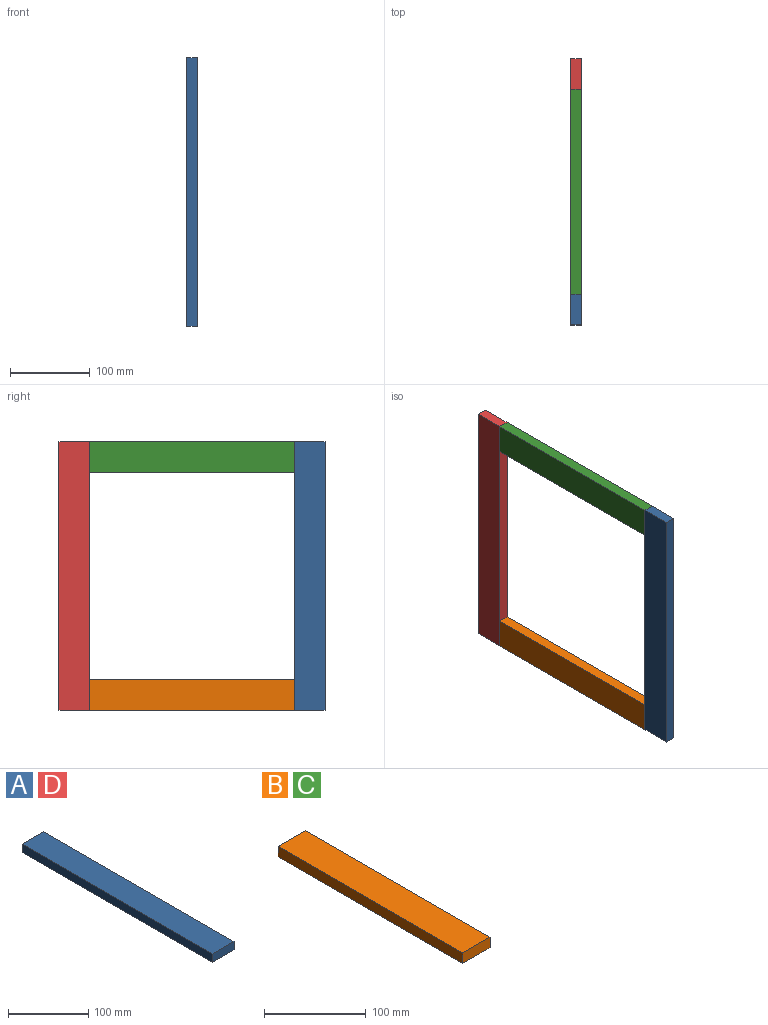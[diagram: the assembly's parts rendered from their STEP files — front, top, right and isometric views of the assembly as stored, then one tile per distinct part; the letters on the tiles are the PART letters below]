
ASSEMBLY  parts=4 mates=9
PART A: 6 faces, bbox 38.1x336.6x12.7 mm
  f0: plane 336.55x12.7mm, normal (-1,0,0), area 4274.2mm2, adj f1,f3,f4,f5
  f1: plane 336.55x38.1mm, normal (0,0,-1), area 12822.6mm2, adj f0,f2,f4,f5
  f2: plane 336.55x12.7mm, normal (1,0,0), area 4274.2mm2, adj f1,f3,f4,f5
  f3: plane 336.55x38.1mm, normal (0,0,1), area 12822.6mm2, adj f0,f2,f4,f5
  f4: plane 38.1x12.7mm, normal (0,-1,0), area 483.9mm2, adj f0,f1,f2,f3
  f5: plane 38.1x12.7mm, normal (0,1,0), area 483.9mm2, adj f0,f1,f2,f3
PART B: 6 faces, bbox 38.1x257.2x12.7 mm
  f0: plane 257.18x38.1mm, normal (0,0,1), area 9798.4mm2, adj f1,f3,f4,f5
  f1: plane 257.18x12.7mm, normal (-1,0,0), area 3266.1mm2, adj f0,f2,f4,f5
  f2: plane 257.18x38.1mm, normal (0,0,-1), area 9798.4mm2, adj f1,f3,f4,f5
  f3: plane 257.18x12.7mm, normal (1,0,0), area 3266.1mm2, adj f0,f2,f4,f5
  f4: plane 38.1x12.7mm, normal (0,-1,0), area 483.9mm2, adj f0,f1,f2,f3
  f5: plane 38.1x12.7mm, normal (0,1,0), area 483.9mm2, adj f0,f1,f2,f3
PART C: same geometry as B
PART D: same geometry as A
PLACE A rot(axis=(0.58,-0.58,-0.58),120deg) t=(71.12,-199.05,117.43)mm
PLACE B rot(axis=(0,1,0),90deg) t=(-21.59,58.12,-181.02)mm
PLACE C rot(axis=(0,1,0),90deg) t=(-21.59,58.12,117.43)mm
PLACE D rot(axis=(-0.58,0.58,-0.58),120deg) t=(-58.42,96.22,-219.12)mm
MATE planar D.f5 <-> B.f3  axis (0,0,-1) through (6.35,77.17,-219.12)mm
MATE planar B.f4 <-> A.f0  axis (0,-1,0) through (6.35,-199.05,-200.07)mm
MATE planar D.f2 <-> B.f5  axis (0,-1,0) through (6.35,58.12,-50.84)mm
MATE planar A.f0 <-> C.f4  axis (0,1,0) through (6.35,-199.05,-50.84)mm
MATE planar B.f0 <-> C.f0  axis (1,0,0) through (12.7,-70.47,-200.07)mm
MATE planar B.f3 <-> A.f4  axis (0,0,-1) through (6.35,-70.47,-219.12)mm
MATE planar C.f1 <-> A.f5  axis (0,0,1) through (0,-70.47,117.43)mm
MATE planar A.f1 <-> B.f0  axis (1,0,0) through (12.7,-218.1,-50.84)mm
MATE planar B.f0 <-> D.f3  axis (1,0,0) through (12.7,58.12,-219.12)mm
